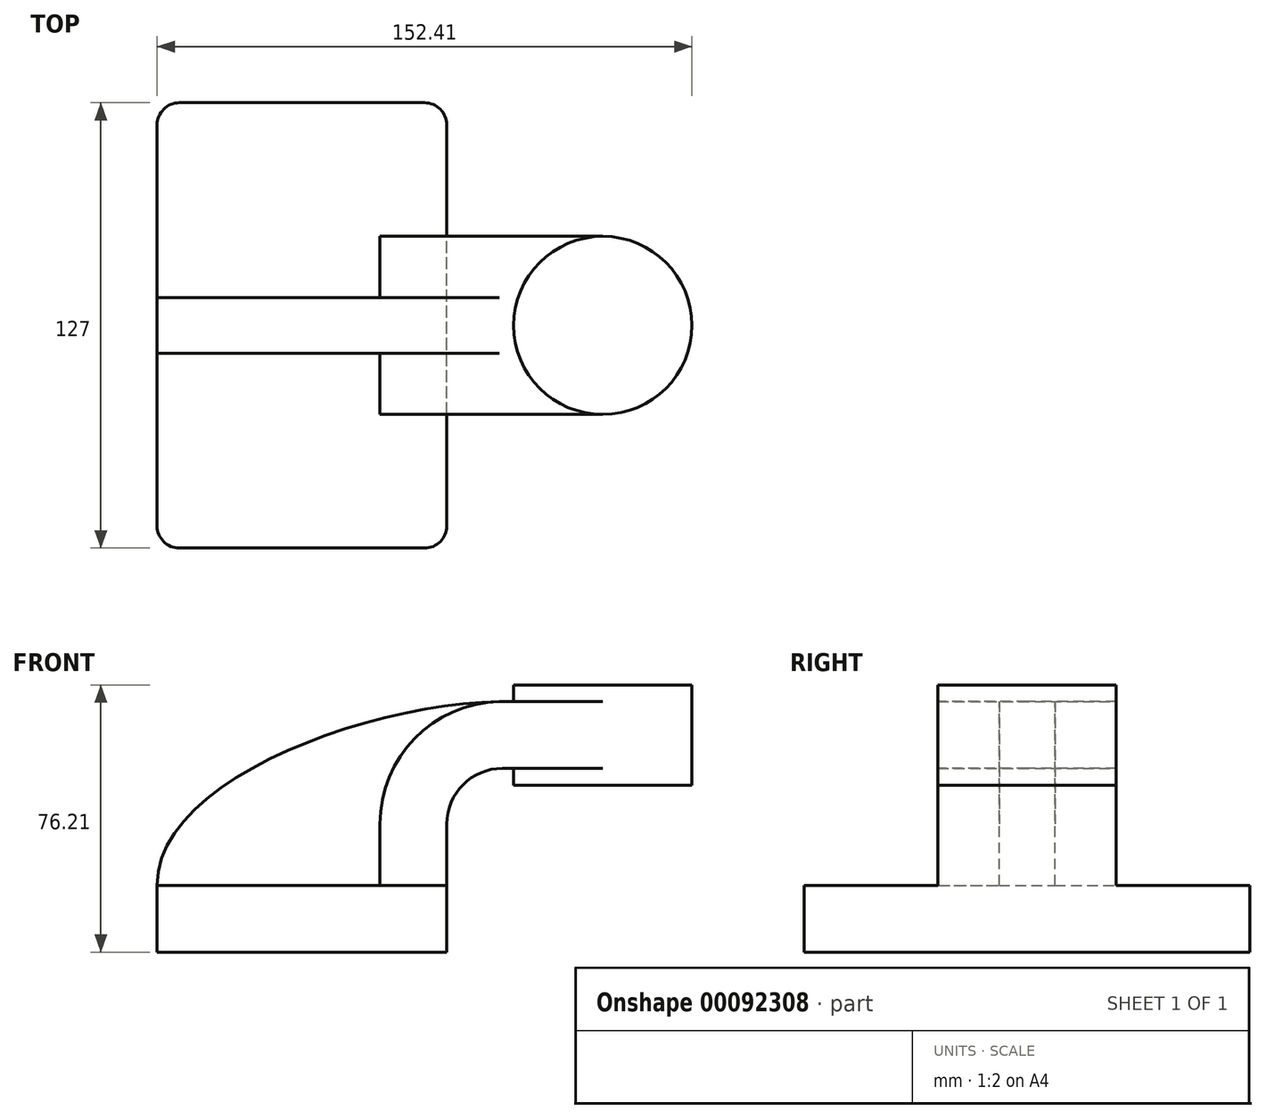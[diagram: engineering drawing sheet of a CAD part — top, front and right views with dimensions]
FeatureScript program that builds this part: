
annotation { "Feature Type Name" : "Feature", "Feature Type Description" : "" }
export const myFeature = defineFeature(function(context is Context, id is Id, definition is map)
    precondition{}
    {
        {
            var Q0;
            Q0=qCreatedBy(makeId("Front.planeOp"),FACE);
            var sketch = newSketch(context, id + "F0", { "sketchPlane" : qUnion([Q0])});
            skLineSegment(sketch, "E0.bottom", {"start": v(41.28, -9.52) * mm, "end": v(-41.28, -9.53) * mm});
            skLineSegment(sketch, "E0.top", {"start": v(41.28, 9.53) * mm, "end": v(-41.28, 9.53) * mm});
            skLineSegment(sketch, "E0.left", {"start": v(41.28, -9.52) * mm, "end": v(41.28, 9.53) * mm});
            skLineSegment(sketch, "E0.right", {"start": v(-41.28, -9.53) * mm, "end": v(-41.28, 9.53) * mm});
            skPoint(sketch, "E0.middle", {"position": v(0, 0) * mm});
            skLineSegment(sketch, "E1.bottom", {"start": v(111.12, 38.1) * mm, "end": v(60.32, 38.1) * mm});
            skLineSegment(sketch, "E1.top", {"start": v(111.12, 66.68) * mm, "end": v(60.32, 66.68) * mm});
            skLineSegment(sketch, "E1.left", {"start": v(111.12, 38.1) * mm, "end": v(111.12, 66.68) * mm});
            skLineSegment(sketch, "E1.right", {"start": v(60.32, 38.1) * mm, "end": v(60.32, 66.68) * mm});
            skPoint(sketch, "E1.middle", {"position": v(85.72, 52.39) * mm});
            skLineSegment(sketch, "E2", {"start": v(41.28, 9.53) * mm, "end": v(41.28, 27) * mm});
            skArc(sketch, "E3", {"start": v(41.27, 27) * mm, "mid": v(45.92, 38.23) * mm, "end": v(57.15, 42.88) * mm});
            skLineSegment(sketch, "E4", {"start": v(57.15, 42.88) * mm, "end": v(85.72, 42.88) * mm});
            skLineSegment(sketch, "E5.0", {"start": v(57.15, 61.93) * mm, "end": v(85.72, 61.93) * mm});
            skArc(sketch, "E5.1", {"start": v(22.23, 27) * mm, "mid": v(32.45, 51.7) * mm, "end": v(57.15, 61.93) * mm});
            skLineSegment(sketch, "E5.2", {"start": v(22.22, 9.53) * mm, "end": v(22.22, 27) * mm});
            skLineSegment(sketch, "E6", {"start": v(85.72, 38.1) * mm, "end": v(85.72, 66.68) * mm});
            skFitSpline(sketch, "E7", {"points": [v(-41.28, 9.53) * mm, v(57.15, 61.93) * mm], "startDerivative": vector(-0.96, 90.77) * mm, "endDerivative": vector(112.46, 0.93) * mm});
            skSolve(sketch);
        }
        {
            var Q0;
            Q0=makeQuery(id+"F0.imprint","IMPRINT",FACE,{"disambiguationData":[TD([[makeQuery(id+"F0.imprint","IMPRINT",EDGE,{"derivedFrom":sQuery(id+"F0.wireOp",EDGE,"E0.bottom")}),-1.0]])]});
            extrude(context, id + "F1", {"entities" : qUnion([Q0]), "endBound" : BoundingType.SYMMETRIC, "depth" : 127 * mm});
        }
        {
            var Q0;
            {var subQ1=sQuery(id+"F0.wireOp",EDGE,"E2");Q0=makeQuery(id+"F0.imprint","IMPRINT",FACE,{"disambiguationData":[TD([[makeQuery(id+"F0.imprint","IMPRINT",EDGE,{"derivedFrom":subQ1}),1.0]])]});}
            var Q1;
            {var subQ0=sQuery(id+"F0.wireOp",EDGE,"E4");var subQ1=sQuery(id+"F0.wireOp",EDGE,"E1.right");var subQ2=makeQuery(id+"F0.imprint","INTERSECT",VERTEX,{"derivedFrom":[subQ1,subQ0]});Q1=makeQuery(id+"F0.imprint","IMPRINT",FACE,{"disambiguationData":[TD([[makeQuery(id+"F0.imprint","IMPRINT",EDGE,{"disambiguationData":[TD([[subQ2,-1.0]])],"derivedFrom":subQ1}),-1.0]])]});}
            extrude(context, id + "F2", {"entities" : qUnion([Q0, Q1]), "operationType" : NewBodyOperationType.ADD, "endBound" : BoundingType.SYMMETRIC, "depth" : 50.8 * mm});
        }
        {
            var Q0;
            {var subQ3=sQuery(id+"F0.wireOp",EDGE,"E5.2");Q0=makeQuery(id+"F0.imprint","IMPRINT",FACE,{"disambiguationData":[TD([[makeQuery(id+"F0.imprint","IMPRINT",EDGE,{"derivedFrom":subQ3}),1.0]])]});}
            extrude(context, id + "F3", {"entities" : qUnion([Q0]), "operationType" : NewBodyOperationType.ADD, "endBound" : BoundingType.SYMMETRIC, "depth" : 15.88 * mm});
        }
        {
            var Q0;
            {var subQ0=sQuery(id+"F0.wireOp",EDGE,"E1.left");Q0=makeQuery(id+"F0.imprint","IMPRINT",FACE,{"disambiguationData":[TD([[makeQuery(id+"F0.imprint","IMPRINT",EDGE,{"derivedFrom":subQ0}),1.0]])]});}
            var Q1;
            Q1=sQuery(id+"F0.wireOp",EDGE,"E6");
            revolve(context, id + "F4", {"operationType" : NewBodyOperationType.ADD, "entities" : qUnion([Q0]), "axis" : qUnion([Q1]), "revolveType" : RevolveType.FULL});
        }
        {
            var Q0;
            Q0=makeQuery(id+"F1.opExtrude","CAP_EDGE",EDGE,{"disambiguationData":[OSD([sQuery(id+"F0.wireOp",EDGE,"E0.right")])],"isStart":false});
            var Q1;
            Q1=makeQuery(id+"F1.opExtrude","CAP_EDGE",EDGE,{"disambiguationData":[OSD([sQuery(id+"F0.wireOp",EDGE,"E0.left")])],"isStart":false});
            var Q2;
            Q2=makeQuery(id+"F1.opExtrude","CAP_EDGE",EDGE,{"disambiguationData":[OSD([sQuery(id+"F0.wireOp",EDGE,"E0.left")])],"isStart":true});
            var Q3;
            Q3=makeQuery(id+"F1.opExtrude","CAP_EDGE",EDGE,{"disambiguationData":[OSD([sQuery(id+"F0.wireOp",EDGE,"E0.right")])],"isStart":true});
            fillet(context, id + "F5", {"entities" : qUnion([Q0, Q1, Q2, Q3]), "radius" : 6.35 * mm, "tangentPropagation" : true, "allowEdgeOverflow" : false});
        }
    });
